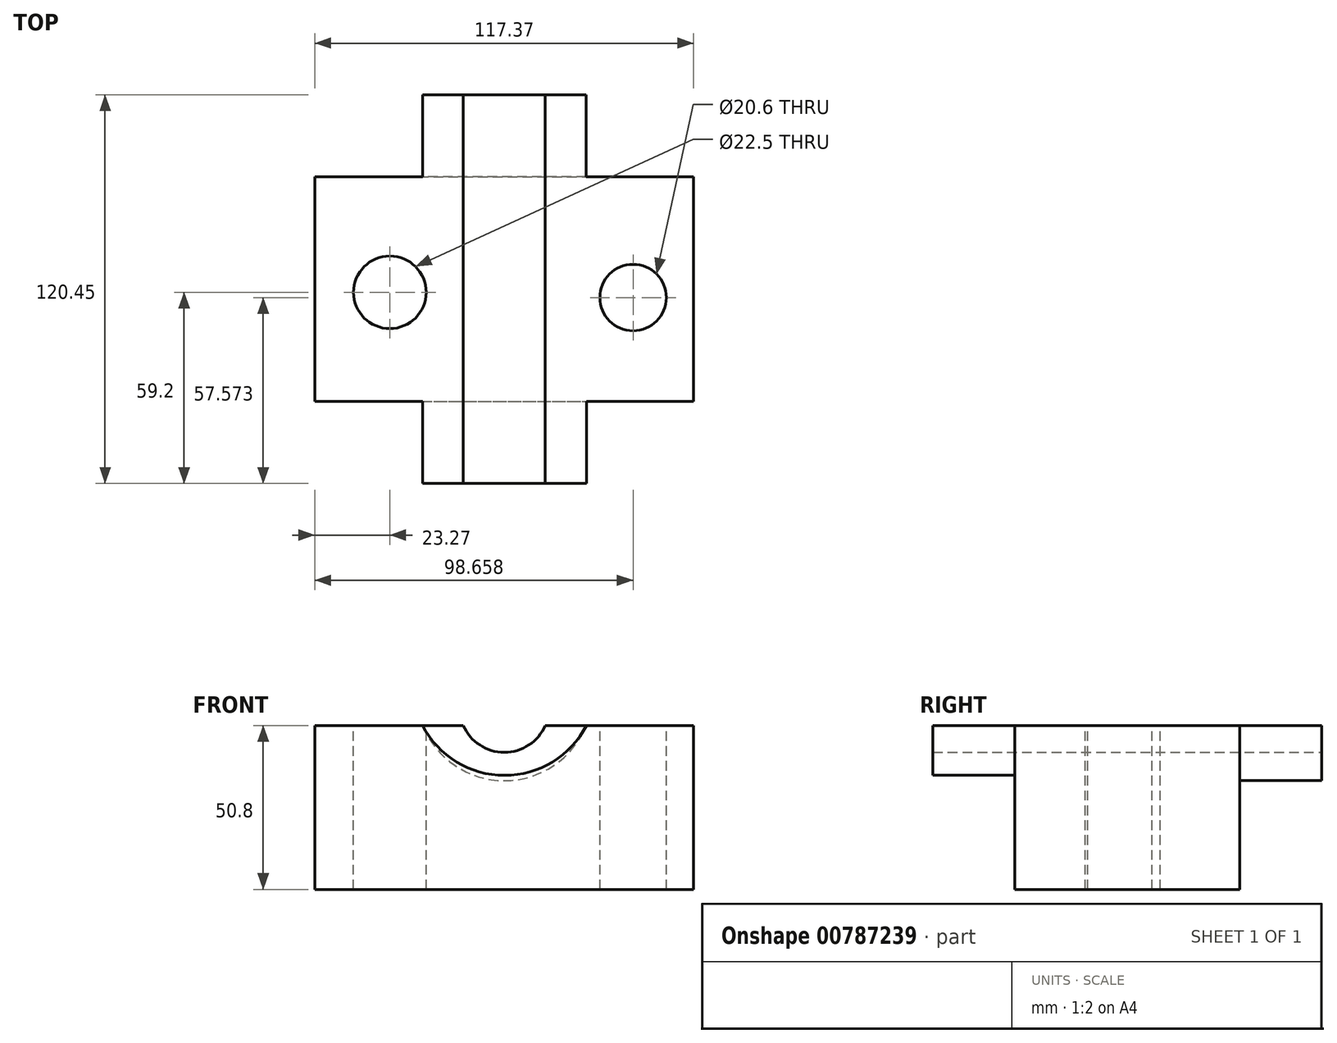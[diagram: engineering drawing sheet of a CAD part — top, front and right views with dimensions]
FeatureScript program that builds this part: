
annotation { "Feature Type Name" : "Feature", "Feature Type Description" : "" }
export const myFeature = defineFeature(function(context is Context, id is Id, definition is map)
    precondition{}
    {
        {
            var Q0;
            Q0=qCreatedBy(makeId("Top.planeOp"),FACE);
            var sketch = newSketch(context, id + "F0", { "sketchPlane" : qUnion([Q0])});
            skLineSegment(sketch, "E0.bottom", {"start": v(-43.96, 40.51) * mm, "end": v(73.41, 40.51) * mm});
            skLineSegment(sketch, "E0.top", {"start": v(-43.96, -29.14) * mm, "end": v(73.41, -29.14) * mm});
            skLineSegment(sketch, "E0.left", {"start": v(-43.96, 40.51) * mm, "end": v(-43.96, -29.14) * mm});
            skLineSegment(sketch, "E0.right", {"start": v(73.41, 40.51) * mm, "end": v(73.41, -29.14) * mm});
            skSolve(sketch);
        }
        {
            var Q0;
            Q0=makeQuery(id+"F0.imprint","IMPRINT",FACE,{"disambiguationData":[TD([[makeQuery(id+"F0.imprint","IMPRINT",EDGE,{"derivedFrom":sQuery(id+"F0.wireOp",EDGE,"E0.bottom")}),-1.0]])]});
            extrude(context, id + "F1", {"entities" : qUnion([Q0]), "depth" : 50.8 * mm, "offsetDistance" : 25.4 * mm});
        }
        {
            var Q0;
            Q0=makeQuery(id+"F1.opExtrude","SWEPT_FACE",FACE,{"disambiguationData":[OSD([sQuery(id+"F0.wireOp",EDGE,"E0.top")])]});
            var sketch = newSketch(context, id + "F2", { "sketchPlane" : qUnion([Q0])});
            skArc(sketch, "E1", {"start": v(-10.56, 50.8) * mm, "mid": v(14.85, 35.34) * mm, "end": v(40.25, 50.8) * mm});
            skArc(sketch, "E2", {"start": v(2.08, 50.8) * mm, "mid": v(14.78, 42.45) * mm, "end": v(27.49, 50.8) * mm});
            skSolve(sketch);
        }
        {
            var Q0;
            Q0 = qSketchRegion(id + "F2", true);
            var Q1;
            {var subQ0=sQuery(id+"F2.wireOp",EDGE,"E1");Q1=makeQuery(id+"F2.imprint","IMPRINT",FACE,{"disambiguationData":[TD([[makeQuery(id+"F2.imprint","IMPRINT",EDGE,{"derivedFrom":subQ0}),1.0]])]});}
            extrude(context, id + "F3", {"entities" : qUnion([Q0, Q1]), "operationType" : NewBodyOperationType.ADD, "depth" : 25.4 * mm, "offsetDistance" : 25.4 * mm});
        }
        {
            var Q0;
            {var subQ0=sQuery(id+"F0.wireOp",EDGE,"E0.top");var subQ3=sQuery(id+"F2.wireOp",EDGE,"E2");Q0=makeQuery(id+"F3.boolean.opBoolean","SPLIT",FACE,{"disambiguationData":[TD([makeQuery(id+"F3.opExtrude","SWEPT_FACE",FACE,{"disambiguationData":[OSD([subQ3])]})])],"derivedFrom":makeQuery(id+"F1.opExtrude","SWEPT_FACE",FACE,{"disambiguationData":[OSD([subQ0])]})});}
            extrude(context, id + "F4", {"entities" : qUnion([Q0]), "operationType" : NewBodyOperationType.REMOVE, "oppositeDirection" : true, "depth" : 82.8 * mm, "offsetDistance" : 25.4 * mm});
        }
        {
            var Q0;
            Q0=makeQuery(id+"F1.opExtrude","SWEPT_FACE",FACE,{"disambiguationData":[OSD([sQuery(id+"F0.wireOp",EDGE,"E0.bottom")])]});
            var sketch = newSketch(context, id + "F5", { "sketchPlane" : qUnion([Q0])});
            skLineSegment(sketch, "E3", {"start": v(-27.49, 50.8) * mm, "end": v(-40.16, 50.8) * mm});
            skLineSegment(sketch, "E4", {"start": v(-2.08, 50.8) * mm, "end": v(10.57, 50.8) * mm});
            skArc(sketch, "E5", {"start": v(-40.16, 50.8) * mm, "mid": v(-14.8, 33.69) * mm, "end": v(10.57, 50.8) * mm});
            skSolve(sketch);
        }
        {
            var Q0;
            Q0 = qSketchRegion(id + "F5", true);
            var Q1;
            Q1=makeQuery(id+"F5.imprint","IMPRINT",FACE,{"disambiguationData":[TD([[makeQuery(id+"F5.imprint","IMPRINT",EDGE,{"derivedFrom":sQuery(id+"F5.wireOp",EDGE,"E3")}),1.0]])]});
            extrude(context, id + "F6", {"entities" : qUnion([Q0, Q1]), "operationType" : NewBodyOperationType.ADD, "depth" : 25.4 * mm, "offsetDistance" : 25.4 * mm});
        }
        {
            var Q0;
            {var subQ0=sQuery(id+"F0.wireOp",EDGE,"E0.left");var subQ2=sQuery(id+"F2.wireOp",EDGE,"E1");var subQ3=sQuery(id+"F0.wireOp",EDGE,"E0.top");var subQ4=sQuery(id+"F0.wireOp",EDGE,"E0.bottom");var subQ5=makeQuery(id+"F1.opExtrude","CAP_EDGE",EDGE,{"disambiguationData":[OSD([subQ3])],"isStart":false});Q0=makeQuery(id+"F6.boolean.opBoolean","MERGE",FACE,{"derivedFrom":[makeQuery(id+"F4.boolean.opBoolean","SPLIT",FACE,{"disambiguationData":[TD([makeQuery(id+"F1.opExtrude","SWEPT_FACE",FACE,{"disambiguationData":[OSD([subQ0])]})])],"derivedFrom":makeQuery(id+"F3.boolean.opBoolean","MERGE",FACE,{"derivedFrom":[makeQuery(id+"F1.opExtrude","CAP_FACE",FACE,{"disambiguationData":[OSD([subQ4,subQ3,subQ0,sQuery(id+"F0.wireOp",EDGE,"E0.right")])],"isStart":false}),makeQuery(id+"F3.opExtrude","SWEPT_FACE",FACE,{"disambiguationData":[OSD([subQ3]),TDD([makeQuery(id+"F2.imprint","IMPRINT",EDGE,{"disambiguationData":[TD([[makeQuery(id+"F2.imprint","INTERSECT",VERTEX,{"disambiguationData":[OD(0.0)],"derivedFrom":[subQ5,subQ2]}),-1.0]])],"derivedFrom":subQ5})])]}),makeQuery(id+"F3.opExtrude","SWEPT_FACE",FACE,{"disambiguationData":[OSD([subQ3]),TDD([makeQuery(id+"F2.imprint","IMPRINT",EDGE,{"disambiguationData":[TD([[makeQuery(id+"F2.imprint","INTERSECT",VERTEX,{"disambiguationData":[OD(1.0)],"derivedFrom":[subQ5,subQ2]}),1.0]])],"derivedFrom":subQ5})])]})]})}),makeQuery(id+"F6.opExtrude","SWEPT_FACE",FACE,{"disambiguationData":[OSD([sQuery(id+"F5.wireOp",EDGE,"E4")])]})]});}
            var sketch = newSketch(context, id + "F7", { "sketchPlane" : qUnion([Q0])});
            skCircle(sketch, "E6", {"center": v(-20.7, 4.66) * mm, "radius": 11.25 * mm});
            skSolve(sketch);
        }
        {
            var Q0;
            {var subQ0=sQuery(id+"F2.wireOp",EDGE,"E1");var subQ1=sQuery(id+"F0.wireOp",EDGE,"E0.top");var subQ3=sQuery(id+"F0.wireOp",EDGE,"E0.right");var subQ4=sQuery(id+"F0.wireOp",EDGE,"E0.bottom");var subQ5=makeQuery(id+"F1.opExtrude","CAP_EDGE",EDGE,{"disambiguationData":[OSD([subQ1])],"isStart":false});Q0=makeQuery(id+"F6.boolean.opBoolean","MERGE",FACE,{"derivedFrom":[makeQuery(id+"F4.boolean.opBoolean","SPLIT",FACE,{"disambiguationData":[TD([makeQuery(id+"F1.opExtrude","SWEPT_FACE",FACE,{"disambiguationData":[OSD([subQ3])]})])],"derivedFrom":makeQuery(id+"F3.boolean.opBoolean","MERGE",FACE,{"derivedFrom":[makeQuery(id+"F1.opExtrude","CAP_FACE",FACE,{"disambiguationData":[OSD([subQ4,subQ1,sQuery(id+"F0.wireOp",EDGE,"E0.left"),subQ3])],"isStart":false}),makeQuery(id+"F3.opExtrude","SWEPT_FACE",FACE,{"disambiguationData":[OSD([subQ1]),TDD([makeQuery(id+"F2.imprint","IMPRINT",EDGE,{"disambiguationData":[TD([[makeQuery(id+"F2.imprint","INTERSECT",VERTEX,{"disambiguationData":[OD(0.0)],"derivedFrom":[subQ5,subQ0]}),-1.0]])],"derivedFrom":subQ5})])]}),makeQuery(id+"F3.opExtrude","SWEPT_FACE",FACE,{"disambiguationData":[OSD([subQ1]),TDD([makeQuery(id+"F2.imprint","IMPRINT",EDGE,{"disambiguationData":[TD([[makeQuery(id+"F2.imprint","INTERSECT",VERTEX,{"disambiguationData":[OD(1.0)],"derivedFrom":[subQ5,subQ0]}),1.0]])],"derivedFrom":subQ5})])]})]})}),makeQuery(id+"F6.opExtrude","SWEPT_FACE",FACE,{"disambiguationData":[OSD([sQuery(id+"F5.wireOp",EDGE,"E3")])]})]});}
            var sketch = newSketch(context, id + "F8", { "sketchPlane" : qUnion([Q0])});
            skCircle(sketch, "E7", {"center": v(54.7, 3.03) * mm, "radius": 10.3 * mm});
            skSolve(sketch);
        }
        {
            var Q0;
            Q0=makeQuery(id+"F8.imprint","IMPRINT",FACE,{"disambiguationData":[TD([[makeQuery(id+"F8.imprint","IMPRINT",EDGE,{"derivedFrom":sQuery(id+"F8.wireOp",EDGE,"E7")}),1.0]])]});
            extrude(context, id + "F9", {"entities" : qUnion([Q0]), "operationType" : NewBodyOperationType.REMOVE, "oppositeDirection" : true, "depth" : 146.56 * mm, "offsetDistance" : 25.4 * mm});
        }
        {
            var Q0;
            Q0=makeQuery(id+"F7.imprint","IMPRINT",FACE,{"disambiguationData":[TD([[makeQuery(id+"F7.imprint","IMPRINT",EDGE,{"derivedFrom":sQuery(id+"F7.wireOp",EDGE,"E6")}),1.0]])]});
            extrude(context, id + "F10", {"entities" : qUnion([Q0]), "operationType" : NewBodyOperationType.REMOVE, "oppositeDirection" : true, "depth" : 101.6 * mm, "offsetDistance" : 25.4 * mm});
        }
    });
